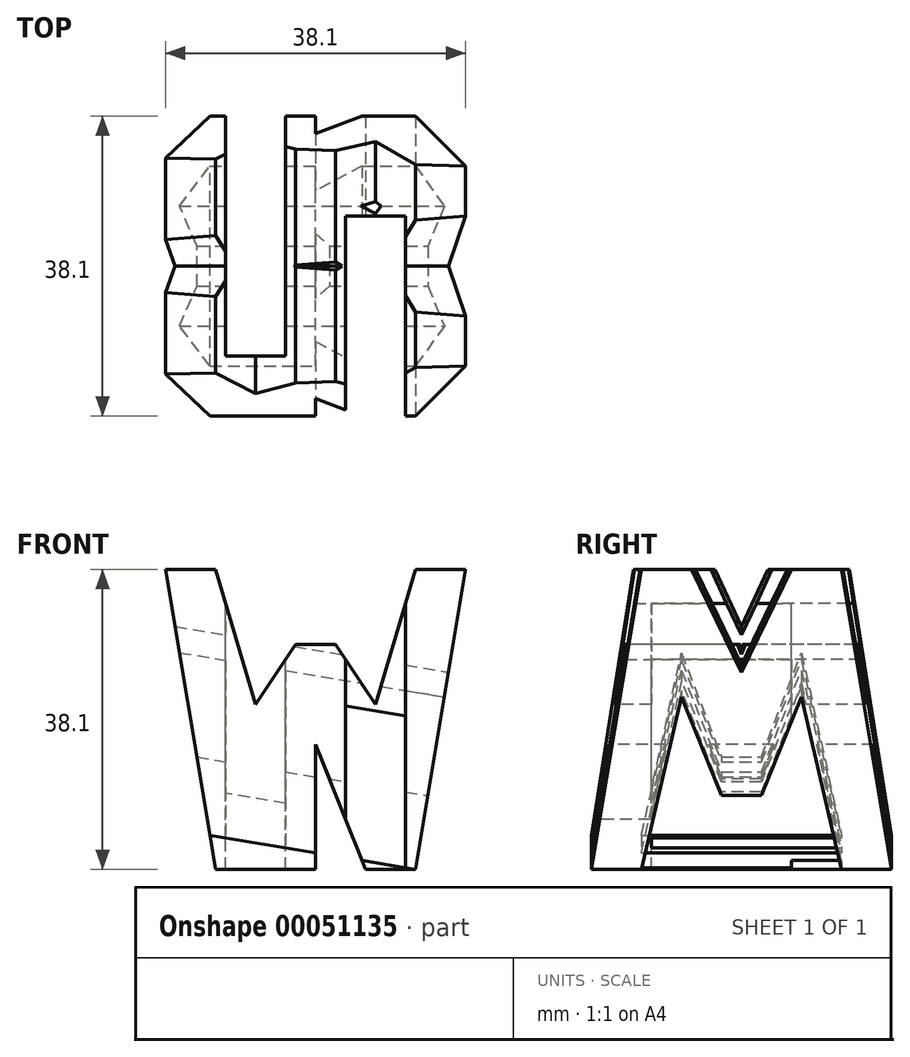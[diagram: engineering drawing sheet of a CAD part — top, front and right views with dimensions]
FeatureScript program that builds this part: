
annotation { "Feature Type Name" : "Feature", "Feature Type Description" : "" }
export const myFeature = defineFeature(function(context is Context, id is Id, definition is map)
    precondition{}
    {
        {
            var Q0;
            Q0=qCreatedBy(makeId("Front.planeOp"),FACE);
            var sketch = newSketch(context, id + "F0", { "sketchPlane" : qUnion([Q0])});
            skLineSegment(sketch, "E0.bottom", {"start": v(0, 0) * mm, "end": v(38.1, 0) * mm});
            skLineSegment(sketch, "E0.top", {"start": v(0, 38.1) * mm, "end": v(38.1, 38.1) * mm});
            skLineSegment(sketch, "E0.left", {"start": v(0, 0) * mm, "end": v(0, 38.1) * mm});
            skLineSegment(sketch, "E0.right", {"start": v(38.1, 0) * mm, "end": v(38.1, 38.1) * mm});
            skSolve(sketch);
        }
        {
            var Q0;
            Q0=makeQuery(id+"F0.imprint","IMPRINT",FACE,{"disambiguationData":[TD([[makeQuery(id+"F0.imprint","IMPRINT",EDGE,{"derivedFrom":sQuery(id+"F0.wireOp",EDGE,"E0.bottom")}),1.0]])]});
            extrude(context, id + "F1", {"entities" : qUnion([Q0]), "depth" : 38.1 * mm});
        }
        {
            var Q0;
            Q0=makeQuery(id+"F1.opExtrude","CAP_FACE",FACE,{"disambiguationData":[OSD([sQuery(id+"F0.wireOp",EDGE,"E0.bottom"),sQuery(id+"F0.wireOp",EDGE,"E0.top"),sQuery(id+"F0.wireOp",EDGE,"E0.left"),sQuery(id+"F0.wireOp",EDGE,"E0.right")])],"isStart":false});
            var sketch = newSketch(context, id + "F2", { "sketchPlane" : qUnion([Q0])});
            skLineSegment(sketch, "E1.bottom", {"start": v(0, 0) * mm, "end": v(38.1, 0) * mm});
            skLineSegment(sketch, "E1.top", {"start": v(0, 38.1) * mm, "end": v(38.1, 38.1) * mm});
            skLineSegment(sketch, "E1.left", {"start": v(0, 0) * mm, "end": v(0, 38.1) * mm});
            skLineSegment(sketch, "E1.right", {"start": v(38.1, 0) * mm, "end": v(38.1, 38.1) * mm});
            skLineSegment(sketch, "E2", {"start": v(0, 38.1) * mm, "end": v(6.35, 0) * mm});
            skLineSegment(sketch, "E3", {"start": v(6.35, 38.1) * mm, "end": v(11.43, 20.95) * mm});
            skLineSegment(sketch, "E4", {"start": v(11.43, 20.95) * mm, "end": v(16.5, 28.57) * mm});
            skLineSegment(sketch, "E5", {"start": v(16.5, 28.57) * mm, "end": v(21.59, 28.57) * mm});
            skLineSegment(sketch, "E6", {"start": v(21.59, 28.57) * mm, "end": v(26.67, 20.95) * mm});
            skLineSegment(sketch, "E7", {"start": v(26.67, 20.95) * mm, "end": v(31.75, 38.1) * mm});
            skLineSegment(sketch, "E8", {"start": v(38.1, 38.1) * mm, "end": v(31.75, 0) * mm});
            skLineSegment(sketch, "E9", {"start": v(25.4, 0) * mm, "end": v(19.05, 15.87) * mm});
            skLineSegment(sketch, "E10", {"start": v(19.05, 15.87) * mm, "end": v(12.7, 0) * mm});
            skLineSegment(sketch, "E11", {"start": v(12.7, 0) * mm, "end": v(19.05, 15.87) * mm});
            skLineSegment(sketch, "E12", {"start": v(19.05, 15.87) * mm, "end": v(19.05, 0) * mm});
            skSolve(sketch);
        }
        {
            var Q0;
            {var subQ0=sQuery(id+"F2.wireOp",EDGE,"E3");Q0=makeQuery(id+"F2.imprint","IMPRINT",FACE,{"disambiguationData":[TD([[makeQuery(id+"F2.imprint","IMPRINT",EDGE,{"derivedFrom":subQ0}),1.0]])]});}
            var Q1;
            {var subQ0=sQuery(id+"F2.wireOp",EDGE,"E1.left");Q1=makeQuery(id+"F2.imprint","IMPRINT",FACE,{"disambiguationData":[TD([[makeQuery(id+"F2.imprint","IMPRINT",EDGE,{"derivedFrom":subQ0}),-1.0]])]});}
            var Q2;
            {var subQ0=sQuery(id+"F2.wireOp",EDGE,"E9");Q2=makeQuery(id+"F2.imprint","IMPRINT",FACE,{"disambiguationData":[TD([[makeQuery(id+"F2.imprint","IMPRINT",EDGE,{"derivedFrom":subQ0}),1.0]])]});}
            var Q3;
            {var subQ0=sQuery(id+"F2.wireOp",EDGE,"E11");Q3=makeQuery(id+"F2.imprint","IMPRINT",FACE,{"disambiguationData":[TD([[makeQuery(id+"F2.imprint","IMPRINT",EDGE,{"derivedFrom":subQ0}),-1.0]])]});}
            var Q4;
            {var subQ0=sQuery(id+"F2.wireOp",EDGE,"E1.right");Q4=makeQuery(id+"F2.imprint","IMPRINT",FACE,{"disambiguationData":[TD([[makeQuery(id+"F2.imprint","IMPRINT",EDGE,{"derivedFrom":subQ0}),1.0]])]});}
            extrude(context, id + "F3", {"entities" : qUnion([Q0, Q1, Q2, Q3, Q4]), "operationType" : NewBodyOperationType.REMOVE, "oppositeDirection" : true, "depth" : 38.1 * mm});
        }
        {
            var Q0;
            Q0=makeQuery(id+"F3.boolean.opBoolean","COPY",FACE,{"derivedFrom":makeQuery(id+"F3.opExtrude","SWEPT_FACE",FACE,{"disambiguationData":[OSD([sQuery(id+"F2.wireOp",EDGE,"E8")])]})});
            var sketch = newSketch(context, id + "F4", { "sketchPlane" : qUnion([Q0])});
            skLineSegment(sketch, "E13.bottom", {"start": v(-38.1, 43.85) * mm, "end": v(0, 43.85) * mm});
            skLineSegment(sketch, "E13.top", {"start": v(-38.1, 5.22) * mm, "end": v(0, 5.22) * mm});
            skLineSegment(sketch, "E13.left", {"start": v(-38.1, 43.85) * mm, "end": v(-38.1, 5.22) * mm});
            skLineSegment(sketch, "E13.right", {"start": v(0, 43.85) * mm, "end": v(0, 5.22) * mm});
            skLineSegment(sketch, "E14", {"start": v(-31.75, 43.85) * mm, "end": v(-38.1, 5.22) * mm});
            skLineSegment(sketch, "E15", {"start": v(-25.4, 43.85) * mm, "end": v(-19.05, 30.62) * mm});
            skLineSegment(sketch, "E16", {"start": v(-19.05, 30.62) * mm, "end": v(-12.7, 43.85) * mm});
            skLineSegment(sketch, "E17", {"start": v(-6.35, 43.85) * mm, "end": v(0, 5.22) * mm});
            skLineSegment(sketch, "E18", {"start": v(-6.35, 5.22) * mm, "end": v(-11.43, 27.44) * mm});
            skLineSegment(sketch, "E19", {"start": v(-11.43, 27.44) * mm, "end": v(-16.51, 14.74) * mm});
            skLineSegment(sketch, "E20", {"start": v(-16.51, 14.74) * mm, "end": v(-21.6, 14.74) * mm});
            skLineSegment(sketch, "E21", {"start": v(-21.6, 14.74) * mm, "end": v(-26.67, 27.44) * mm});
            skLineSegment(sketch, "E22", {"start": v(-26.67, 27.44) * mm, "end": v(-31.75, 5.22) * mm});
            skLineSegment(sketch, "E23", {"start": v(-19.05, 30.62) * mm, "end": v(-19.05, 43.85) * mm});
            skSolve(sketch);
        }
        {
            var Q0;
            {var subQ0=sQuery(id+"F4.wireOp",EDGE,"E13.right");Q0=makeQuery(id+"F4.imprint","IMPRINT",FACE,{"disambiguationData":[TD([[makeQuery(id+"F4.imprint","IMPRINT",EDGE,{"derivedFrom":subQ0}),-1.0]])]});}
            var Q1;
            {var subQ0=sQuery(id+"F4.wireOp",EDGE,"E16");Q1=makeQuery(id+"F4.imprint","IMPRINT",FACE,{"disambiguationData":[TD([[makeQuery(id+"F4.imprint","IMPRINT",EDGE,{"derivedFrom":subQ0}),1.0]])]});}
            var Q2;
            {var subQ0=sQuery(id+"F4.wireOp",EDGE,"E15");Q2=makeQuery(id+"F4.imprint","IMPRINT",FACE,{"disambiguationData":[TD([[makeQuery(id+"F4.imprint","IMPRINT",EDGE,{"derivedFrom":subQ0}),1.0]])]});}
            var Q3;
            {var subQ1=sQuery(id+"F4.wireOp",EDGE,"E18");Q3=makeQuery(id+"F4.imprint","IMPRINT",FACE,{"disambiguationData":[TD([[makeQuery(id+"F4.imprint","IMPRINT",EDGE,{"derivedFrom":subQ1}),1.0]])]});}
            var Q4;
            {var subQ0=sQuery(id+"F4.wireOp",EDGE,"E13.left");Q4=makeQuery(id+"F4.imprint","IMPRINT",FACE,{"disambiguationData":[TD([[makeQuery(id+"F4.imprint","IMPRINT",EDGE,{"derivedFrom":subQ0}),1.0]])]});}
            extrude(context, id + "F5", {"entities" : qUnion([Q0, Q1, Q2, Q3, Q4]), "operationType" : NewBodyOperationType.REMOVE, "oppositeDirection" : true, "depth" : 38.1 * mm});
        }
        {
            var Q0;
            Q0=qCreatedBy(makeId("Top.planeOp"),FACE);
            cPlane(context, id + "F6", {"entities" : qUnion([Q0]), "cplaneType" : CPlaneType.OFFSET, "offset" : 38.1 * mm, "width" : 152.4 * mm, "height" : 152.4 * mm});
        }
        {
            var Q0;
            Q0=qCreatedBy(id+"F6.planeOp",FACE);
            var sketch = newSketch(context, id + "F7", { "sketchPlane" : qUnion([Q0])});
            skLineSegment(sketch, "E24.bottom", {"start": v(38.1, 0) * mm, "end": v(0, 0) * mm});
            skLineSegment(sketch, "E24.top", {"start": v(38.1, -38.1) * mm, "end": v(0, -38.1) * mm});
            skLineSegment(sketch, "E24.left", {"start": v(38.1, 0) * mm, "end": v(38.1, -38.1) * mm});
            skLineSegment(sketch, "E24.right", {"start": v(0, 0) * mm, "end": v(0, -38.1) * mm});
            skLineSegment(sketch, "E25", {"start": v(30.48, -12.7) * mm, "end": v(30.48, -38.1) * mm});
            skLineSegment(sketch, "E26", {"start": v(30.48, -12.7) * mm, "end": v(22.86, -12.7) * mm});
            skLineSegment(sketch, "E27", {"start": v(22.86, -12.7) * mm, "end": v(22.86, -38.1) * mm});
            skLineSegment(sketch, "E28", {"start": v(15.24, -30.48) * mm, "end": v(15.24, 0) * mm});
            skLineSegment(sketch, "E29", {"start": v(15.24, -30.48) * mm, "end": v(7.62, -30.48) * mm});
            skLineSegment(sketch, "E30", {"start": v(7.62, -30.48) * mm, "end": v(7.62, 0) * mm});
            skSolve(sketch);
        }
        {
            var Q0;
            {var subQ0=sQuery(id+"F7.wireOp",EDGE,"E25");Q0=makeQuery(id+"F7.imprint","IMPRINT",FACE,{"disambiguationData":[TD([[makeQuery(id+"F7.imprint","IMPRINT",EDGE,{"derivedFrom":subQ0}),-1.0]])]});}
            var Q1;
            {var subQ0=sQuery(id+"F7.wireOp",EDGE,"E28");Q1=makeQuery(id+"F7.imprint","IMPRINT",FACE,{"disambiguationData":[TD([[makeQuery(id+"F7.imprint","IMPRINT",EDGE,{"derivedFrom":subQ0}),1.0]])]});}
            extrude(context, id + "F8", {"entities" : qUnion([Q0, Q1]), "operationType" : NewBodyOperationType.REMOVE, "oppositeDirection" : true, "depth" : 38.1 * mm});
        }
    });
